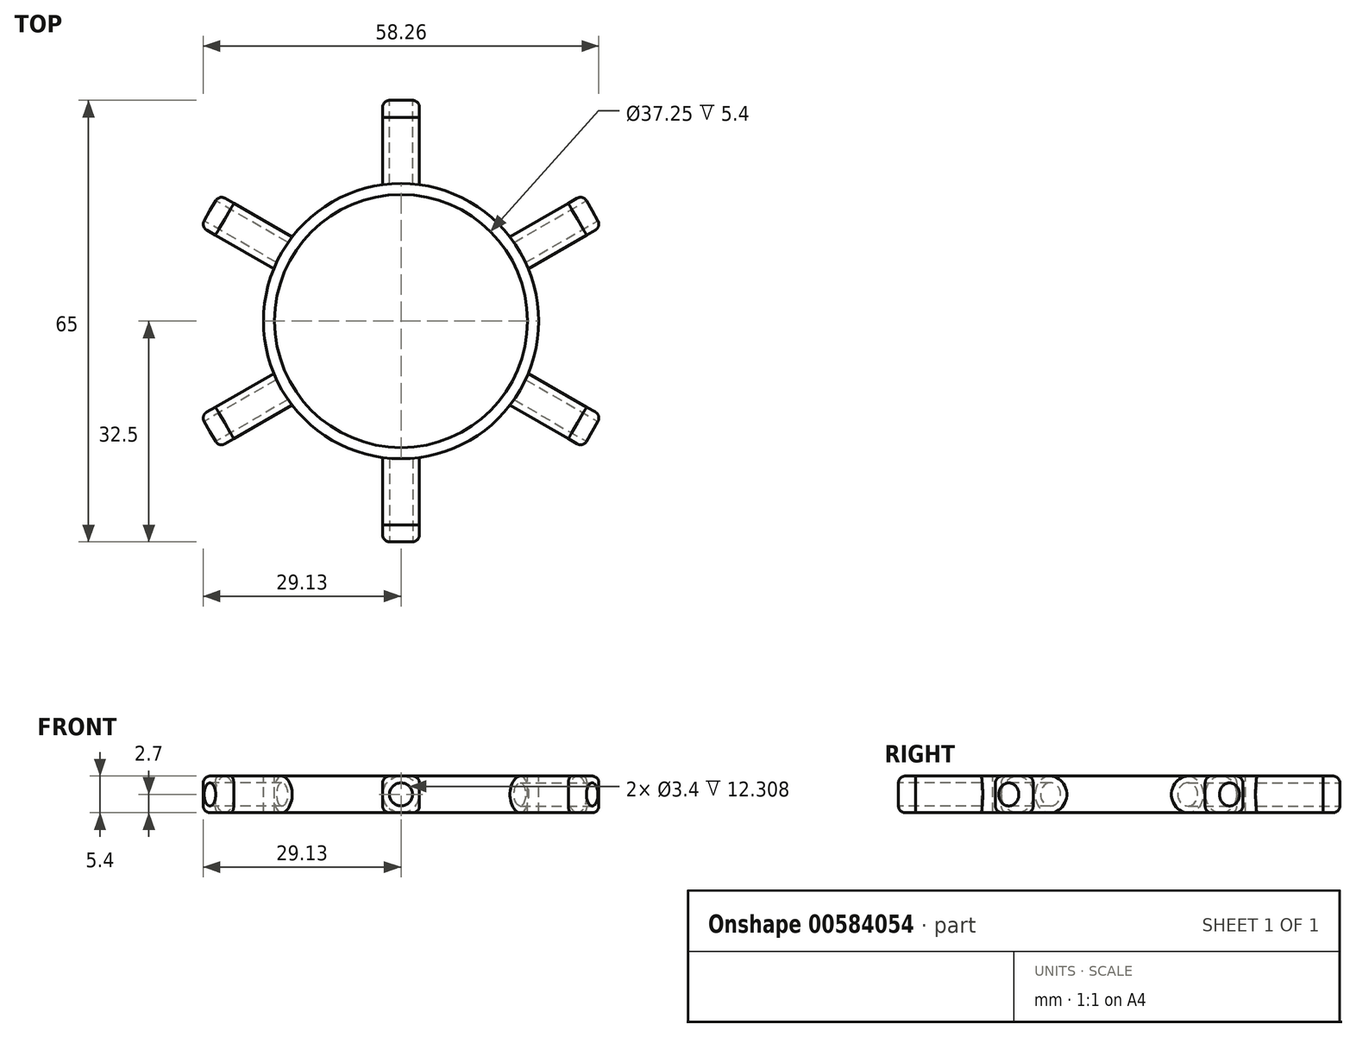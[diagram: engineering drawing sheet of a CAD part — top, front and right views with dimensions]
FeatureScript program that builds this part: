
annotation { "Feature Type Name" : "Feature", "Feature Type Description" : "" }
export const myFeature = defineFeature(function(context is Context, id is Id, definition is map)
    precondition{}
    {
        {
            var Q0;
            Q0=qCreatedBy(makeId("Front.planeOp"),FACE);
            var sketch = newSketch(context, id + "F0", { "sketchPlane" : qUnion([Q0])});
            skCircle(sketch, "E0", {"center": v(0, 0) * mm, "radius": 1.7 * mm});
            skCircle(sketch, "E1", {"center": v(0, 0) * mm, "radius": 2.7 * mm});
            skSolve(sketch);
        }
        {
            var Q0;
            Q0=makeQuery(id+"F0.imprint","IMPRINT",FACE,{"disambiguationData":[TD([[makeQuery(id+"F0.imprint","IMPRINT",EDGE,{"derivedFrom":sQuery(id+"F0.wireOp",EDGE,"E0")}),1.0]])]});
            var sketch = newSketch(context, id + "F1", { "sketchPlane" : qUnion([Q0])});
            skLineSegment(sketch, "E2.bottom", {"start": v(-2.7, 2.7) * mm, "end": v(2.7, 2.7) * mm});
            skLineSegment(sketch, "E2.top", {"start": v(-2.7, -2.7) * mm, "end": v(2.7, -2.7) * mm});
            skLineSegment(sketch, "E2.left", {"start": v(-2.7, 2.7) * mm, "end": v(-2.7, -2.7) * mm});
            skLineSegment(sketch, "E2.right", {"start": v(2.7, 2.7) * mm, "end": v(2.7, -2.7) * mm});
            skPoint(sketch, "E2.middle", {"position": v(0, 0) * mm});
            skSolve(sketch);
        }
        {
            var Q0;
            Q0=makeQuery(id+"F0.imprint","IMPRINT",FACE,{"disambiguationData":[TD([[makeQuery(id+"F0.imprint","IMPRINT",EDGE,{"derivedFrom":sQuery(id+"F0.wireOp",EDGE,"E0")}),-1.0]])]});
            extrude(context, id + "F2", {"entities" : qUnion([Q0]), "depth" : 10 * mm, "offsetDistance" : 25 * mm});
        }
        {
            var Q0;
            Q0=makeQuery(id+"F1.imprint","IMPRINT",FACE,{"disambiguationData":[TD([[makeQuery(id+"F1.imprint","IMPRINT",EDGE,{"derivedFrom":sQuery(id+"F1.wireOp",EDGE,"E2.bottom")}),-1.0]])]});
            extrude(context, id + "F3", {"entities" : qUnion([Q0]), "operationType" : NewBodyOperationType.ADD, "depth" : -2.5 * mm, "offsetDistance" : 25 * mm});
        }
        {
            var Q0;
            Q0=makeQuery(id+"F3.opExtrude","SWEPT_EDGE",EDGE,{"disambiguationData":[OSD([sQuery(id+"F1.wireOp",EDGE,"E2.bottom"),sQuery(id+"F1.wireOp",EDGE,"E2.left")])]});
            var Q1;
            Q1=makeQuery(id+"F3.opExtrude","SWEPT_EDGE",EDGE,{"disambiguationData":[OSD([sQuery(id+"F1.wireOp",EDGE,"E2.bottom"),sQuery(id+"F1.wireOp",EDGE,"E2.right")])]});
            var Q2;
            Q2=makeQuery(id+"F3.opExtrude","SWEPT_EDGE",EDGE,{"disambiguationData":[OSD([sQuery(id+"F1.wireOp",EDGE,"E2.top"),sQuery(id+"F1.wireOp",EDGE,"E2.right")])]});
            var Q3;
            Q3=makeQuery(id+"F3.opExtrude","CAP_EDGE",EDGE,{"disambiguationData":[OSD([sQuery(id+"F1.wireOp",EDGE,"E2.top")])],"isStart":false});
            var Q4;
            Q4=makeQuery(id+"F3.opExtrude","CAP_EDGE",EDGE,{"disambiguationData":[OSD([sQuery(id+"F1.wireOp",EDGE,"E2.left")])],"isStart":false});
            var Q5;
            Q5=makeQuery(id+"F3.opExtrude","CAP_EDGE",EDGE,{"disambiguationData":[OSD([sQuery(id+"F1.wireOp",EDGE,"E2.right")])],"isStart":false});
            var Q6;
            Q6=makeQuery(id+"F3.opExtrude","CAP_EDGE",EDGE,{"disambiguationData":[OSD([sQuery(id+"F1.wireOp",EDGE,"E2.bottom")])],"isStart":false});
            var Q7;
            Q7=makeQuery(id+"F3.opExtrude","SWEPT_EDGE",EDGE,{"disambiguationData":[OSD([sQuery(id+"F1.wireOp",EDGE,"E2.top"),sQuery(id+"F1.wireOp",EDGE,"E2.left")])]});
            fillet(context, id + "F4", {"entities" : qUnion([Q0, Q1, Q2, Q3, Q4, Q5, Q6, Q7]), "radius" : 1 * mm, "tangentPropagation" : true, "allowEdgeOverflow" : false});
        }
        {
            var Q0;
            Q0=makeQuery(id+"F2.opExtrude","SWEPT_BODY",BODY,{"disambiguationData":[OSD([sQuery(id+"F0.wireOp",EDGE,"E0"),sQuery(id+"F0.wireOp",EDGE,"E1")])]});
            transform(context, id + "F5", {"entities" : qUnion([Q0]), "transformType" : TransformType.TRANSLATION_3D, "dx" : 0 * mm, "dy" : 30 * mm, "dz" : 0 * mm, "makeCopy" : false});
        }
        {
            var Q0;
            Q0=qCreatedBy(makeId("Front.planeOp"),FACE);
            var sketch = newSketch(context, id + "F6", { "sketchPlane" : qUnion([Q0])});
            skLineSegment(sketch, "E3", {"start": v(0, 46.42) * mm, "end": v(0, -39.08) * mm});
            skSolve(sketch);
        }
        {
            var Q0;
            Q0=makeQuery(id+"F2.opExtrude","SWEPT_BODY",BODY,{"disambiguationData":[OSD([sQuery(id+"F0.wireOp",EDGE,"E0"),sQuery(id+"F0.wireOp",EDGE,"E1")])]});
            var Q1;
            Q1=sQuery(id+"F6.wireOp",EDGE,"E3");
            circularPattern(context, id + "F7", {"operationType" : NewBodyOperationType.ADD, "entities" : qUnion([Q0]), "axis" : qUnion([Q1]), "angle" : 360 * degree, "instanceCount" : 6, "equalSpace" : true});
        }
        {
            var Q0;
            Q0=makeQuery(id+"F7.opPattern","COPY",FACE,{"derivedFrom":makeQuery(id+"F3.opExtrude","SWEPT_FACE",FACE,{"disambiguationData":[OSD([sQuery(id+"F1.wireOp",EDGE,"E2.bottom")])]}),"instanceName":"4"});
            var sketch = newSketch(context, id + "F8", { "sketchPlane" : qUnion([Q0])});
            skCircle(sketch, "E4", {"center": v(0, 0) * mm, "radius": 20.26 * mm});
            skCircle(sketch, "E5", {"center": v(0, 0) * mm, "radius": 18.62 * mm});
            skSolve(sketch);
        }
        {
            var Q0;
            Q0 = qSketchRegion(id + "F8", true);
            var Q1;
            Q1=makeQuery(id+"F7.opPattern","COPY",FACE,{"derivedFrom":makeQuery(id+"F3.opExtrude","SWEPT_FACE",FACE,{"disambiguationData":[OSD([sQuery(id+"F1.wireOp",EDGE,"E2.top")])]}),"instanceName":"5"});
            extrude(context, id + "F9", {"entities" : qUnion([Q0]), "operationType" : NewBodyOperationType.ADD, "endBound" : BoundingType.UP_TO_SURFACE, "oppositeDirection" : true, "depth" : 25 * mm, "endBoundEntityFace" : qUnion([Q1]), "offsetDistance" : 25 * mm});
        }
    });
